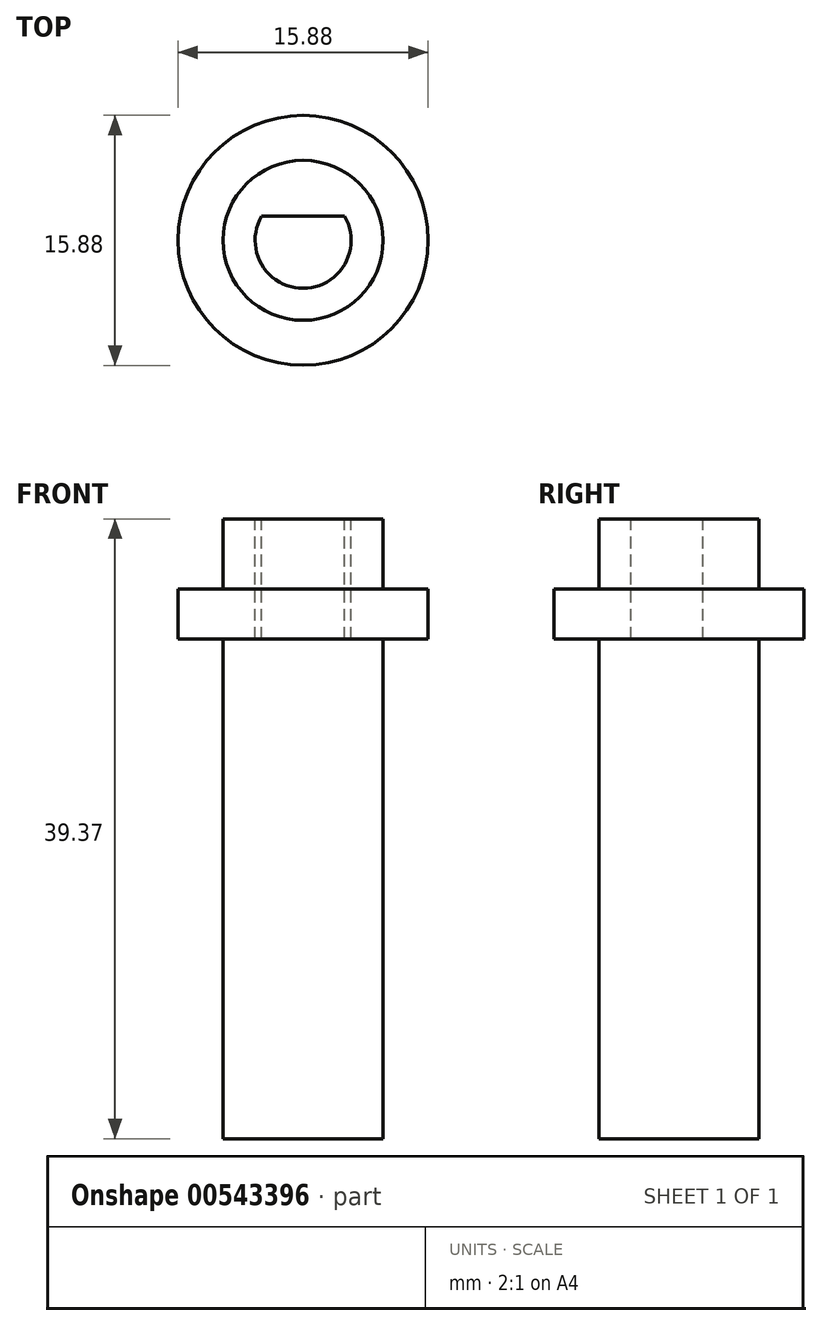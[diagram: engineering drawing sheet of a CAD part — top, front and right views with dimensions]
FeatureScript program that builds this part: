
annotation { "Feature Type Name" : "Feature", "Feature Type Description" : "" }
export const myFeature = defineFeature(function(context is Context, id is Id, definition is map)
    precondition{}
    {
        {
            var Q0;
            Q0=qCreatedBy(makeId("Front.planeOp"),FACE);
            var sketch = newSketch(context, id + "F0", { "sketchPlane" : qUnion([Q0])});
            skLineSegment(sketch, "E0", {"start": v(0, 17.58) * mm, "end": v(0, -14.85) * mm, "construction": true});
            skLineSegment(sketch, "E1", {"start": v(0, 7.62) * mm, "end": v(5.08, 7.62) * mm});
            skLineSegment(sketch, "E2", {"start": v(5.08, 7.62) * mm, "end": v(5.08, 3.17) * mm});
            skLineSegment(sketch, "E3", {"start": v(5.08, 3.17) * mm, "end": v(7.94, 3.18) * mm});
            skLineSegment(sketch, "E4", {"start": v(7.94, 3.18) * mm, "end": v(7.94, 0) * mm});
            skLineSegment(sketch, "E5", {"start": v(7.94, 0) * mm, "end": v(5.08, 0) * mm});
            skLineSegment(sketch, "E6", {"start": v(5.08, 0) * mm, "end": v(5.08, -31.75) * mm});
            skLineSegment(sketch, "E7", {"start": v(5.08, -31.75) * mm, "end": v(0, -31.75) * mm});
            skLineSegment(sketch, "E8", {"start": v(0, -31.75) * mm, "end": v(0, 7.62) * mm});
            skSolve(sketch);
        }
        {
            var Q0;
            Q0 = qSketchRegion(id + "F0", true);
            var Q1;
            Q1=sQuery(id+"F0.wireOp",EDGE,"E0");
            revolve(context, id + "F1", {"entities" : qUnion([Q0]), "axis" : qUnion([Q1]), "revolveType" : RevolveType.FULL});
        }
        {
            var Q0;
            Q0=makeQuery(id+"F1.opRevolve","SWEPT_FACE",FACE,{"disambiguationData":[OSD([sQuery(id+"F0.wireOp",EDGE,"E1")])]});
            var sketch = newSketch(context, id + "F2", { "sketchPlane" : qUnion([Q0])});
            skCircle(sketch, "E9", {"center": v(0, 0) * mm, "radius": 3.05 * mm});
            skLineSegment(sketch, "E10", {"start": v(-2.64, 1.52) * mm, "end": v(2.64, 1.52) * mm});
            skSolve(sketch);
        }
        {
            var Q0;
            {var subQ0=sQuery(id+"F2.wireOp",EDGE,"E10");Q0=makeQuery(id+"F2.imprint","IMPRINT",FACE,{"disambiguationData":[TD([[makeQuery(id+"F2.imprint","IMPRINT",EDGE,{"derivedFrom":subQ0}),-1.0]])]});}
            extrude(context, id + "F3", {"entities" : qUnion([Q0]), "operationType" : NewBodyOperationType.REMOVE, "oppositeDirection" : true, "depth" : 7.62 * mm, "offsetDistance" : 25.4 * mm});
        }
    });
